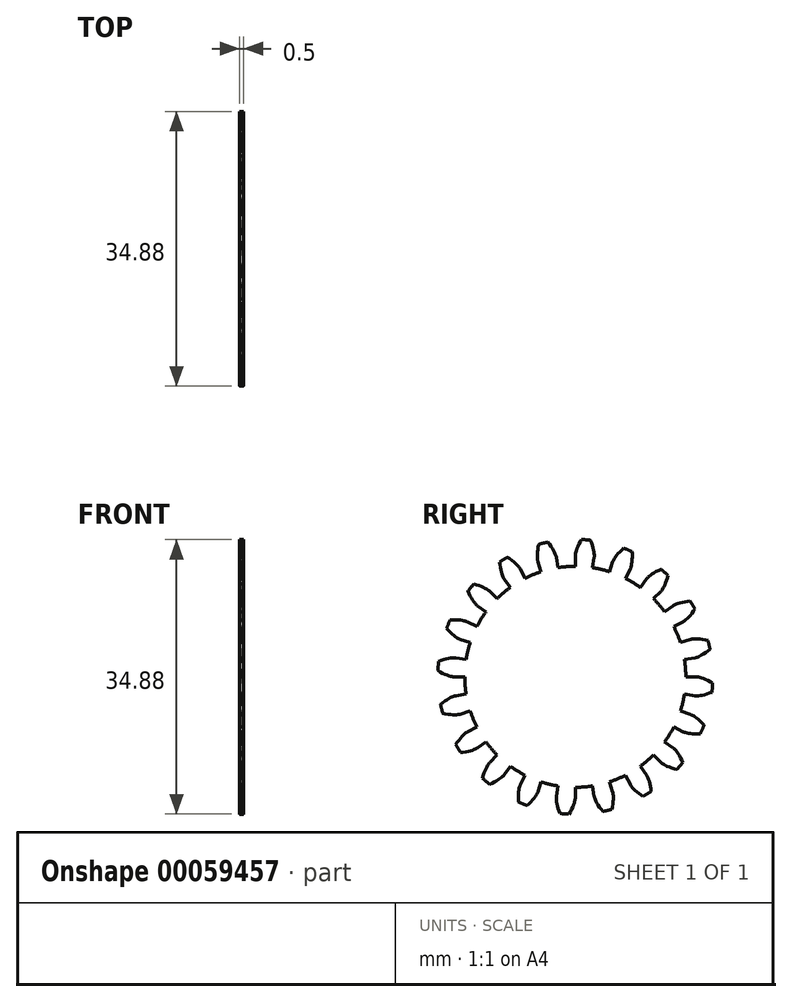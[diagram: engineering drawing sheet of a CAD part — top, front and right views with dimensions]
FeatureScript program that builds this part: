
annotation { "Feature Type Name" : "Feature", "Feature Type Description" : "" }
export const myFeature = defineFeature(function(context is Context, id is Id, definition is map)
    precondition{}
    {
        {
            assignVariable(context, id + "F0", {"name" : "GearThickness", "anyValue" : .5});
        }
        {
            var Q0;
            Q0=qCreatedBy(makeId("Right.planeOp"),FACE);
            var sketch = newSketch(context, id + "F1", { "sketchPlane" : qUnion([Q0])});
            skCircle(sketch, "E0", {"center": v(0, 0) * mm, "radius": 14.04 * mm});
            skCircle(sketch, "E1", {"center": v(0, 0) * mm, "radius": 15.37 * mm, "construction": true});
            skCircle(sketch, "E2", {"center": v(0, 0) * mm, "radius": 15.88 * mm, "construction": true});
            skCircle(sketch, "E3", {"center": v(0, 0) * mm, "radius": 17.46 * mm});
            skLineSegment(sketch, "E4", {"start": v(0, 0) * mm, "end": v(-15.37, 0) * mm, "construction": true});
            skLineSegment(sketch, "E5.1.0", {"start": v(0, 0) * mm, "end": v(-15.35, 0.77) * mm, "construction": true});
            skLineSegment(sketch, "E5.2.0", {"start": v(0, 0) * mm, "end": v(-15.3, 1.53) * mm, "construction": true});
            skLineSegment(sketch, "E5.3.0", {"start": v(0, 0) * mm, "end": v(-15.2, 2.3) * mm, "construction": true});
            skLineSegment(sketch, "E5.4.0", {"start": v(0, 0) * mm, "end": v(-15.06, 3.05) * mm, "construction": true});
            skLineSegment(sketch, "E5.5.0", {"start": v(0, 0) * mm, "end": v(-14.9, 3.8) * mm, "construction": true});
            skLineSegment(sketch, "E5.6.0", {"start": v(0, 0) * mm, "end": v(-14.68, 4.54) * mm, "construction": true});
            skLineSegment(sketch, "E5.7.0", {"start": v(0, 0) * mm, "end": v(-14.44, 5.27) * mm, "construction": true});
            skLineSegment(sketch, "E5.8.0", {"start": v(0, 0) * mm, "end": v(-14.16, 5.99) * mm, "construction": true});
            skLineSegment(sketch, "E5.9.0", {"start": v(0, 0) * mm, "end": v(-13.84, 6.69) * mm, "construction": true});
            skLineSegment(sketch, "E5.10.0", {"start": v(0, 0) * mm, "end": v(-13.49, 7.37) * mm, "construction": true});
            skLineSegment(sketch, "E5.11.0", {"start": v(0, 0) * mm, "end": v(-13.1, 8.03) * mm, "construction": true});
            skLineSegment(sketch, "E5.12.0", {"start": v(0, 0) * mm, "end": v(-12.68, 8.68) * mm, "construction": true});
            skLineSegment(sketch, "E5.13.0", {"start": v(0, 0) * mm, "end": v(-12.24, 9.3) * mm, "construction": true});
            skLineSegment(sketch, "E5.14.0", {"start": v(0, 0) * mm, "end": v(-11.76, 9.9) * mm, "construction": true});
            skLineSegment(sketch, "E5.anchor2", {"start": v(0, 0) * mm, "end": v(-11.76, 9.9) * mm, "construction": true});
            skLineSegment(sketch, "E6", {"start": v(-15.35, 0.77) * mm, "end": v(-15.39, 0) * mm, "construction": true});
            skLineSegment(sketch, "E7", {"start": v(-15.3, 1.53) * mm, "end": v(-15.45, 0) * mm, "construction": true});
            skLineSegment(sketch, "E8", {"start": v(-15.2, 2.3) * mm, "end": v(-15.54, 0.02) * mm, "construction": true});
            skLineSegment(sketch, "E9", {"start": v(-14.9, 3.8) * mm, "end": v(-15.84, 0.08) * mm, "construction": true});
            skLineSegment(sketch, "E10", {"start": v(-14.68, 4.54) * mm, "end": v(-16.05, 0.14) * mm, "construction": true});
            skLineSegment(sketch, "E11", {"start": v(-14.44, 5.27) * mm, "end": v(-16.28, 0.22) * mm, "construction": true});
            skLineSegment(sketch, "E12", {"start": v(-14.16, 5.99) * mm, "end": v(-16.55, 0.32) * mm, "construction": true});
            skLineSegment(sketch, "E13", {"start": v(-13.84, 6.69) * mm, "end": v(-16.85, 0.46) * mm, "construction": true});
            skLineSegment(sketch, "E14", {"start": v(-13.49, 7.37) * mm, "end": v(-17.17, 0.62) * mm, "construction": true});
            skLineSegment(sketch, "E15", {"start": v(-13.1, 8.03) * mm, "end": v(-17.52, 0.83) * mm, "construction": true});
            skLineSegment(sketch, "E16", {"start": v(-15.06, 3.05) * mm, "end": v(-15.67, 0.04) * mm, "construction": true});
            skLineSegment(sketch, "E17", {"start": v(-12.68, 8.68) * mm, "end": v(-17.9, 1.07) * mm, "construction": true});
            skLineSegment(sketch, "E18", {"start": v(-12.24, 9.3) * mm, "end": v(-18.28, 1.35) * mm, "construction": true});
            skLineSegment(sketch, "E19", {"start": v(-11.76, 9.9) * mm, "end": v(-18.69, 1.67) * mm, "construction": true});
            skLineSegment(sketch, "E20", {"start": v(0, 0) * mm, "end": v(-15.32, 1.2) * mm, "construction": true});
            skLineSegment(sketch, "E21", {"start": v(-14.04, 0) * mm, "end": v(-15.37, 0) * mm});
            skLineSegment(sketch, "E22.MirrorCS", {"start": v(-13.87, 2.2) * mm, "end": v(-15.18, 2.4) * mm});
            skLineSegment(sketch, "E23", {"start": v(-15.37, 0) * mm, "end": v(-15.39, 0) * mm});
            skLineSegment(sketch, "E24", {"start": v(-15.39, 0) * mm, "end": v(-15.45, 0) * mm});
            skLineSegment(sketch, "E25", {"start": v(-15.45, 0) * mm, "end": v(-15.54, 0.02) * mm});
            skLineSegment(sketch, "E26", {"start": v(-15.54, 0.02) * mm, "end": v(-15.67, 0.04) * mm});
            skLineSegment(sketch, "E27", {"start": v(-15.67, 0.04) * mm, "end": v(-15.84, 0.08) * mm});
            skLineSegment(sketch, "E28", {"start": v(-15.84, 0.08) * mm, "end": v(-16.05, 0.14) * mm});
            skLineSegment(sketch, "E29", {"start": v(-16.05, 0.14) * mm, "end": v(-16.28, 0.22) * mm});
            skLineSegment(sketch, "E30", {"start": v(-16.28, 0.22) * mm, "end": v(-16.55, 0.32) * mm});
            skLineSegment(sketch, "E31", {"start": v(-16.55, 0.32) * mm, "end": v(-16.85, 0.46) * mm});
            skLineSegment(sketch, "E32", {"start": v(-16.85, 0.46) * mm, "end": v(-17.17, 0.62) * mm});
            skLineSegment(sketch, "E33", {"start": v(-17.17, 0.62) * mm, "end": v(-17.52, 0.83) * mm});
            skLineSegment(sketch, "E34", {"start": v(-17.52, 0.83) * mm, "end": v(-17.9, 1.07) * mm});
            skLineSegment(sketch, "E35", {"start": v(-17.9, 1.07) * mm, "end": v(-18.28, 1.35) * mm});
            skLineSegment(sketch, "E36", {"start": v(-18.28, 1.35) * mm, "end": v(-18.69, 1.67) * mm});
            skLineSegment(sketch, "E37.MirrorCS", {"start": v(-15.18, 2.4) * mm, "end": v(-15.2, 2.4) * mm});
            skLineSegment(sketch, "E38.MirrorCS", {"start": v(-15.2, 2.4) * mm, "end": v(-15.26, 2.41) * mm});
            skLineSegment(sketch, "E39.MirrorCS", {"start": v(-15.26, 2.41) * mm, "end": v(-15.35, 2.41) * mm});
            skLineSegment(sketch, "E40.MirrorCS", {"start": v(-15.35, 2.41) * mm, "end": v(-15.49, 2.41) * mm});
            skLineSegment(sketch, "E41.MirrorCS", {"start": v(-15.66, 2.4) * mm, "end": v(-15.87, 2.37) * mm});
            skLineSegment(sketch, "E42.MirrorCS", {"start": v(-15.87, 2.37) * mm, "end": v(-16.12, 2.33) * mm});
            skLineSegment(sketch, "E43.MirrorCS", {"start": v(-16.12, 2.33) * mm, "end": v(-16.4, 2.27) * mm});
            skLineSegment(sketch, "E44.MirrorCS", {"start": v(-16.4, 2.27) * mm, "end": v(-16.71, 2.18) * mm});
            skLineSegment(sketch, "E45.MirrorCS", {"start": v(-17.06, 2.07) * mm, "end": v(-17.43, 1.92) * mm});
            skLineSegment(sketch, "E46.MirrorCS", {"start": v(-16.71, 2.18) * mm, "end": v(-17.06, 2.07) * mm});
            skLineSegment(sketch, "E47.MirrorCS", {"start": v(-17.43, 1.92) * mm, "end": v(-17.84, 1.74) * mm});
            skLineSegment(sketch, "E48.MirrorCS", {"start": v(-17.84, 1.74) * mm, "end": v(-18.27, 1.53) * mm});
            skLineSegment(sketch, "E49.MirrorCS", {"start": v(-18.27, 1.53) * mm, "end": v(-18.72, 1.27) * mm});
            skLineSegment(sketch, "E50.MirrorCS", {"start": v(-15.49, 2.41) * mm, "end": v(-15.66, 2.4) * mm});
            skLineSegment(sketch, "E51.1.0", {"start": v(-13.35, -4.34) * mm, "end": v(-14.62, -4.75) * mm});
            skLineSegment(sketch, "E51.1.1", {"start": v(-17.18, -3.56) * mm, "end": v(-17.5, -3.85) * mm});
            skLineSegment(sketch, "E51.1.2", {"start": v(-13.87, -2.2) * mm, "end": v(-15.18, -2.4) * mm});
            skLineSegment(sketch, "E51.1.3", {"start": v(-16.86, -3.3) * mm, "end": v(-17.18, -3.56) * mm});
            skLineSegment(sketch, "E51.1.4", {"start": v(-16.52, -4.71) * mm, "end": v(-16.92, -4.63) * mm});
            skLineSegment(sketch, "E51.1.5", {"start": v(-16.92, -4.63) * mm, "end": v(-17.35, -4.51) * mm});
            skLineSegment(sketch, "E51.1.6", {"start": v(-16.57, -3.09) * mm, "end": v(-16.86, -3.3) * mm});
            skLineSegment(sketch, "E51.1.7", {"start": v(-17.85, -4.2) * mm, "end": v(-18.2, -4.58) * mm});
            skLineSegment(sketch, "E51.1.8", {"start": v(-16.3, -2.9) * mm, "end": v(-16.57, -3.09) * mm});
            skLineSegment(sketch, "E51.1.9", {"start": v(-17.8, -4.37) * mm, "end": v(-18.29, -4.18) * mm});
            skLineSegment(sketch, "E51.1.10", {"start": v(-17.5, -3.85) * mm, "end": v(-17.85, -4.2) * mm});
            skLineSegment(sketch, "E51.1.11", {"start": v(-16.16, -4.77) * mm, "end": v(-16.52, -4.71) * mm});
            skLineSegment(sketch, "E51.1.12", {"start": v(-17.35, -4.51) * mm, "end": v(-17.8, -4.37) * mm});
            skLineSegment(sketch, "E51.1.13", {"start": v(-15.63, -2.56) * mm, "end": v(-15.83, -2.65) * mm});
            skLineSegment(sketch, "E51.1.14", {"start": v(-15.83, -2.65) * mm, "end": v(-16.05, -2.76) * mm});
            skLineSegment(sketch, "E51.1.15", {"start": v(-16.05, -2.76) * mm, "end": v(-16.3, -2.9) * mm});
            skLineSegment(sketch, "E51.1.16", {"start": v(-15.55, -4.83) * mm, "end": v(-15.84, -4.8) * mm});
            skLineSegment(sketch, "E51.1.17", {"start": v(-15.3, -4.83) * mm, "end": v(-15.55, -4.83) * mm});
            skLineSegment(sketch, "E51.1.18", {"start": v(-15.84, -4.8) * mm, "end": v(-16.16, -4.77) * mm});
            skLineSegment(sketch, "E51.1.19", {"start": v(-15.47, -2.5) * mm, "end": v(-15.63, -2.56) * mm});
            skLineSegment(sketch, "E51.1.20", {"start": v(-15.35, -2.45) * mm, "end": v(-15.47, -2.5) * mm});
            skLineSegment(sketch, "E51.1.21", {"start": v(-15.1, -4.82) * mm, "end": v(-15.3, -4.83) * mm});
            skLineSegment(sketch, "E51.1.22", {"start": v(-14.92, -4.8) * mm, "end": v(-15.1, -4.82) * mm});
            skLineSegment(sketch, "E51.1.23", {"start": v(-14.7, -4.77) * mm, "end": v(-14.79, -4.79) * mm});
            skLineSegment(sketch, "E51.1.24", {"start": v(-15.18, -2.4) * mm, "end": v(-15.2, -2.4) * mm});
            skLineSegment(sketch, "E51.1.25", {"start": v(-15.2, -2.4) * mm, "end": v(-15.26, -2.42) * mm});
            skLineSegment(sketch, "E51.1.26", {"start": v(-14.79, -4.79) * mm, "end": v(-14.92, -4.8) * mm});
            skLineSegment(sketch, "E51.1.27", {"start": v(-15.26, -2.42) * mm, "end": v(-15.35, -2.45) * mm});
            skLineSegment(sketch, "E51.1.28", {"start": v(-14.64, -4.75) * mm, "end": v(-14.7, -4.77) * mm});
            skLineSegment(sketch, "E51.1.29", {"start": v(-14.62, -4.75) * mm, "end": v(-14.64, -4.75) * mm});
            skLineSegment(sketch, "E51.2.0", {"start": v(-11.36, -8.25) * mm, "end": v(-12.43, -9.03) * mm});
            skLineSegment(sketch, "E51.2.1", {"start": v(-15.24, -8.7) * mm, "end": v(-15.46, -9.07) * mm});
            skLineSegment(sketch, "E51.2.2", {"start": v(-12.5, -6.37) * mm, "end": v(-13.7, -6.98) * mm});
            skLineSegment(sketch, "E51.2.3", {"start": v(-15.02, -8.35) * mm, "end": v(-15.24, -8.7) * mm});
            skLineSegment(sketch, "E51.2.4", {"start": v(-14.26, -9.59) * mm, "end": v(-14.66, -9.63) * mm});
            skLineSegment(sketch, "E51.2.5", {"start": v(-14.66, -9.63) * mm, "end": v(-15.1, -9.65) * mm});
            skLineSegment(sketch, "E51.2.6", {"start": v(-14.8, -8.06) * mm, "end": v(-15.02, -8.35) * mm});
            skLineSegment(sketch, "E51.2.7", {"start": v(-15.68, -9.5) * mm, "end": v(-15.89, -9.97) * mm});
            skLineSegment(sketch, "E51.2.8", {"start": v(-14.6, -7.8) * mm, "end": v(-14.8, -8.06) * mm});
            skLineSegment(sketch, "E51.2.9", {"start": v(-15.58, -9.65) * mm, "end": v(-16.1, -9.63) * mm});
            skLineSegment(sketch, "E51.2.10", {"start": v(-15.46, -9.07) * mm, "end": v(-15.68, -9.5) * mm});
            skLineSegment(sketch, "E51.2.11", {"start": v(-13.9, -9.53) * mm, "end": v(-14.26, -9.59) * mm});
            skLineSegment(sketch, "E51.2.12", {"start": v(-15.1, -9.65) * mm, "end": v(-15.58, -9.65) * mm});
            skLineSegment(sketch, "E51.2.13", {"start": v(-14.08, -7.26) * mm, "end": v(-14.23, -7.4) * mm});
            skLineSegment(sketch, "E51.2.14", {"start": v(-14.23, -7.4) * mm, "end": v(-14.4, -7.59) * mm});
            skLineSegment(sketch, "E51.2.15", {"start": v(-14.4, -7.59) * mm, "end": v(-14.6, -7.8) * mm});
            skLineSegment(sketch, "E51.2.16", {"start": v(-13.3, -9.4) * mm, "end": v(-13.58, -9.47) * mm});
            skLineSegment(sketch, "E51.2.17", {"start": v(-13.06, -9.32) * mm, "end": v(-13.3, -9.4) * mm});
            skLineSegment(sketch, "E51.2.18", {"start": v(-13.58, -9.47) * mm, "end": v(-13.9, -9.53) * mm});
            skLineSegment(sketch, "E51.2.19", {"start": v(-13.95, -7.15) * mm, "end": v(-14.08, -7.26) * mm});
            skLineSegment(sketch, "E51.2.20", {"start": v(-13.84, -7.07) * mm, "end": v(-13.95, -7.15) * mm});
            skLineSegment(sketch, "E51.2.21", {"start": v(-12.86, -9.25) * mm, "end": v(-13.06, -9.32) * mm});
            skLineSegment(sketch, "E51.2.22", {"start": v(-12.7, -9.18) * mm, "end": v(-12.86, -9.25) * mm});
            skLineSegment(sketch, "E51.2.23", {"start": v(-12.5, -9.07) * mm, "end": v(-12.58, -9.12) * mm});
            skLineSegment(sketch, "E51.2.24", {"start": v(-13.7, -6.98) * mm, "end": v(-13.71, -6.99) * mm});
            skLineSegment(sketch, "E51.2.25", {"start": v(-13.71, -6.99) * mm, "end": v(-13.76, -7.02) * mm});
            skLineSegment(sketch, "E51.2.26", {"start": v(-12.58, -9.12) * mm, "end": v(-12.7, -9.18) * mm});
            skLineSegment(sketch, "E51.2.27", {"start": v(-13.76, -7.02) * mm, "end": v(-13.84, -7.07) * mm});
            skLineSegment(sketch, "E51.2.28", {"start": v(-12.45, -9.04) * mm, "end": v(-12.5, -9.07) * mm});
            skLineSegment(sketch, "E51.2.29", {"start": v(-12.43, -9.03) * mm, "end": v(-12.45, -9.04) * mm});
            skLineSegment(sketch, "E51.3.0", {"start": v(-8.25, -11.36) * mm, "end": v(-9.03, -12.43) * mm});
            skLineSegment(sketch, "E51.3.1", {"start": v(-11.8, -12.97) * mm, "end": v(-11.9, -13.4) * mm});
            skLineSegment(sketch, "E51.3.2", {"start": v(-9.93, -9.93) * mm, "end": v(-10.87, -10.87) * mm});
            skLineSegment(sketch, "E51.3.3", {"start": v(-11.7, -12.58) * mm, "end": v(-11.8, -12.97) * mm});
            skLineSegment(sketch, "E51.3.4", {"start": v(-10.6, -13.53) * mm, "end": v(-10.97, -13.69) * mm});
            skLineSegment(sketch, "E51.3.5", {"start": v(-10.97, -13.69) * mm, "end": v(-11.38, -13.85) * mm});
            skLineSegment(sketch, "E51.3.6", {"start": v(-11.59, -12.24) * mm, "end": v(-11.7, -12.58) * mm});
            skLineSegment(sketch, "E51.3.7", {"start": v(-11.97, -13.88) * mm, "end": v(-12.03, -14.4) * mm});
            skLineSegment(sketch, "E51.3.8", {"start": v(-11.47, -11.93) * mm, "end": v(-11.59, -12.24) * mm});
            skLineSegment(sketch, "E51.3.9", {"start": v(-11.84, -14) * mm, "end": v(-12.34, -14.13) * mm});
            skLineSegment(sketch, "E51.3.10", {"start": v(-11.9, -13.4) * mm, "end": v(-11.97, -13.88) * mm});
            skLineSegment(sketch, "E51.3.11", {"start": v(-10.27, -13.36) * mm, "end": v(-10.6, -13.53) * mm});
            skLineSegment(sketch, "E51.3.12", {"start": v(-11.38, -13.85) * mm, "end": v(-11.84, -14) * mm});
            skLineSegment(sketch, "E51.3.13", {"start": v(-11.15, -11.26) * mm, "end": v(-11.25, -11.44) * mm});
            skLineSegment(sketch, "E51.3.14", {"start": v(-11.25, -11.44) * mm, "end": v(-11.36, -11.67) * mm});
            skLineSegment(sketch, "E51.3.15", {"start": v(-11.36, -11.67) * mm, "end": v(-11.47, -11.93) * mm});
            skLineSegment(sketch, "E51.3.16", {"start": v(-9.75, -13.04) * mm, "end": v(-9.99, -13.2) * mm});
            skLineSegment(sketch, "E51.3.17", {"start": v(-9.54, -12.9) * mm, "end": v(-9.75, -13.04) * mm});
            skLineSegment(sketch, "E51.3.18", {"start": v(-9.99, -13.2) * mm, "end": v(-10.27, -13.36) * mm});
            skLineSegment(sketch, "E51.3.19", {"start": v(-11.05, -11.11) * mm, "end": v(-11.15, -11.26) * mm});
            skLineSegment(sketch, "E51.3.20", {"start": v(-10.98, -11) * mm, "end": v(-11.05, -11.11) * mm});
            skLineSegment(sketch, "E51.3.21", {"start": v(-9.38, -12.77) * mm, "end": v(-9.54, -12.9) * mm});
            skLineSegment(sketch, "E51.3.22", {"start": v(-9.25, -12.66) * mm, "end": v(-9.38, -12.77) * mm});
            skLineSegment(sketch, "E51.3.23", {"start": v(-9.08, -12.5) * mm, "end": v(-9.15, -12.56) * mm});
            skLineSegment(sketch, "E51.3.24", {"start": v(-10.87, -10.87) * mm, "end": v(-10.88, -10.88) * mm});
            skLineSegment(sketch, "E51.3.25", {"start": v(-10.88, -10.88) * mm, "end": v(-10.92, -10.93) * mm});
            skLineSegment(sketch, "E51.3.26", {"start": v(-9.15, -12.56) * mm, "end": v(-9.25, -12.66) * mm});
            skLineSegment(sketch, "E51.3.27", {"start": v(-10.92, -10.93) * mm, "end": v(-10.98, -11) * mm});
            skLineSegment(sketch, "E51.3.28", {"start": v(-9.05, -12.45) * mm, "end": v(-9.08, -12.5) * mm});
            skLineSegment(sketch, "E51.3.29", {"start": v(-9.03, -12.43) * mm, "end": v(-9.05, -12.45) * mm});
            skLineSegment(sketch, "E51.4.0", {"start": v(-4.34, -13.35) * mm, "end": v(-4.75, -14.62) * mm});
            skLineSegment(sketch, "E51.4.1", {"start": v(-7.22, -15.99) * mm, "end": v(-7.17, -16.43) * mm});
            skLineSegment(sketch, "E51.4.2", {"start": v(-6.37, -12.5) * mm, "end": v(-6.98, -13.7) * mm});
            skLineSegment(sketch, "E51.4.3", {"start": v(-7.24, -15.58) * mm, "end": v(-7.22, -15.99) * mm});
            skLineSegment(sketch, "E51.4.4", {"start": v(-5.9, -16.14) * mm, "end": v(-6.2, -16.4) * mm});
            skLineSegment(sketch, "E51.4.5", {"start": v(-6.2, -16.4) * mm, "end": v(-6.54, -16.69) * mm});
            skLineSegment(sketch, "E51.4.6", {"start": v(-7.24, -15.22) * mm, "end": v(-7.24, -15.58) * mm});
            skLineSegment(sketch, "E51.4.7", {"start": v(-7.1, -16.9) * mm, "end": v(-7, -17.4) * mm});
            skLineSegment(sketch, "E51.4.8", {"start": v(-7.23, -14.9) * mm, "end": v(-7.24, -15.22) * mm});
            skLineSegment(sketch, "E51.4.9", {"start": v(-6.93, -16.97) * mm, "end": v(-7.37, -17.25) * mm});
            skLineSegment(sketch, "E51.4.10", {"start": v(-7.17, -16.43) * mm, "end": v(-7.1, -16.9) * mm});
            skLineSegment(sketch, "E51.4.11", {"start": v(-5.64, -15.88) * mm, "end": v(-5.9, -16.14) * mm});
            skLineSegment(sketch, "E51.4.12", {"start": v(-6.54, -16.69) * mm, "end": v(-6.93, -16.97) * mm});
            skLineSegment(sketch, "E51.4.13", {"start": v(-7.12, -14.15) * mm, "end": v(-7.16, -14.36) * mm});
            skLineSegment(sketch, "E51.4.14", {"start": v(-7.16, -14.36) * mm, "end": v(-7.2, -14.6) * mm});
            skLineSegment(sketch, "E51.4.15", {"start": v(-7.2, -14.6) * mm, "end": v(-7.23, -14.9) * mm});
            skLineSegment(sketch, "E51.4.16", {"start": v(-5.24, -15.42) * mm, "end": v(-5.42, -15.64) * mm});
            skLineSegment(sketch, "E51.4.17", {"start": v(-5.09, -15.22) * mm, "end": v(-5.24, -15.42) * mm});
            skLineSegment(sketch, "E51.4.18", {"start": v(-5.42, -15.64) * mm, "end": v(-5.64, -15.88) * mm});
            skLineSegment(sketch, "E51.4.19", {"start": v(-7.08, -13.98) * mm, "end": v(-7.12, -14.15) * mm});
            skLineSegment(sketch, "E51.4.20", {"start": v(-7.04, -13.86) * mm, "end": v(-7.08, -13.98) * mm});
            skLineSegment(sketch, "E51.4.21", {"start": v(-4.97, -15.04) * mm, "end": v(-5.09, -15.22) * mm});
            skLineSegment(sketch, "E51.4.22", {"start": v(-4.88, -14.9) * mm, "end": v(-4.97, -15.04) * mm});
            skLineSegment(sketch, "E51.4.23", {"start": v(-4.78, -14.69) * mm, "end": v(-4.82, -14.78) * mm});
            skLineSegment(sketch, "E51.4.24", {"start": v(-6.98, -13.7) * mm, "end": v(-6.99, -13.71) * mm});
            skLineSegment(sketch, "E51.4.25", {"start": v(-6.99, -13.71) * mm, "end": v(-7, -13.76) * mm});
            skLineSegment(sketch, "E51.4.26", {"start": v(-4.82, -14.78) * mm, "end": v(-4.88, -14.9) * mm});
            skLineSegment(sketch, "E51.4.27", {"start": v(-7, -13.76) * mm, "end": v(-7.04, -13.86) * mm});
            skLineSegment(sketch, "E51.4.28", {"start": v(-4.76, -14.64) * mm, "end": v(-4.78, -14.69) * mm});
            skLineSegment(sketch, "E51.4.29", {"start": v(-4.75, -14.62) * mm, "end": v(-4.76, -14.64) * mm});
            skLineSegment(sketch, "E51.5.0", {"start": v(0, -14.04) * mm, "end": v(0, -15.37) * mm});
            skLineSegment(sketch, "E51.5.1", {"start": v(-1.92, -17.43) * mm, "end": v(-1.74, -17.84) * mm});
            skLineSegment(sketch, "E51.5.2", {"start": v(-2.2, -13.87) * mm, "end": v(-2.4, -15.18) * mm});
            skLineSegment(sketch, "E51.5.3", {"start": v(-2.07, -17.06) * mm, "end": v(-1.92, -17.43) * mm});
            skLineSegment(sketch, "E51.5.4", {"start": v(-0.62, -17.17) * mm, "end": v(-0.83, -17.52) * mm});
            skLineSegment(sketch, "E51.5.5", {"start": v(-0.83, -17.52) * mm, "end": v(-1.07, -17.9) * mm});
            skLineSegment(sketch, "E51.5.6", {"start": v(-2.18, -16.71) * mm, "end": v(-2.07, -17.06) * mm});
            skLineSegment(sketch, "E51.5.7", {"start": v(-1.53, -18.27) * mm, "end": v(-1.27, -18.72) * mm});
            skLineSegment(sketch, "E51.5.8", {"start": v(-2.27, -16.4) * mm, "end": v(-2.18, -16.71) * mm});
            skLineSegment(sketch, "E51.5.9", {"start": v(-1.35, -18.28) * mm, "end": v(-1.67, -18.69) * mm});
            skLineSegment(sketch, "E51.5.10", {"start": v(-1.74, -17.84) * mm, "end": v(-1.53, -18.27) * mm});
            skLineSegment(sketch, "E51.5.11", {"start": v(-0.46, -16.85) * mm, "end": v(-0.62, -17.17) * mm});
            skLineSegment(sketch, "E51.5.12", {"start": v(-1.07, -17.9) * mm, "end": v(-1.35, -18.28) * mm});
            skLineSegment(sketch, "E51.5.13", {"start": v(-2.4, -15.66) * mm, "end": v(-2.37, -15.87) * mm});
            skLineSegment(sketch, "E51.5.14", {"start": v(-2.37, -15.87) * mm, "end": v(-2.33, -16.12) * mm});
            skLineSegment(sketch, "E51.5.15", {"start": v(-2.33, -16.12) * mm, "end": v(-2.27, -16.4) * mm});
            skLineSegment(sketch, "E51.5.16", {"start": v(-0.22, -16.28) * mm, "end": v(-0.32, -16.55) * mm});
            skLineSegment(sketch, "E51.5.17", {"start": v(-0.14, -16.05) * mm, "end": v(-0.22, -16.28) * mm});
            skLineSegment(sketch, "E51.5.18", {"start": v(-0.32, -16.55) * mm, "end": v(-0.46, -16.85) * mm});
            skLineSegment(sketch, "E51.5.19", {"start": v(-2.41, -15.49) * mm, "end": v(-2.4, -15.66) * mm});
            skLineSegment(sketch, "E51.5.20", {"start": v(-2.41, -15.35) * mm, "end": v(-2.41, -15.49) * mm});
            skLineSegment(sketch, "E51.5.21", {"start": v(-0.08, -15.84) * mm, "end": v(-0.14, -16.05) * mm});
            skLineSegment(sketch, "E51.5.22", {"start": v(-0.04, -15.67) * mm, "end": v(-0.08, -15.84) * mm});
            skLineSegment(sketch, "E51.5.23", {"start": v(0, -15.45) * mm, "end": v(-0.02, -15.54) * mm});
            skLineSegment(sketch, "E51.5.24", {"start": v(-2.4, -15.18) * mm, "end": v(-2.4, -15.2) * mm});
            skLineSegment(sketch, "E51.5.25", {"start": v(-2.4, -15.2) * mm, "end": v(-2.41, -15.26) * mm});
            skLineSegment(sketch, "E51.5.26", {"start": v(-0.02, -15.54) * mm, "end": v(-0.04, -15.67) * mm});
            skLineSegment(sketch, "E51.5.27", {"start": v(-2.41, -15.26) * mm, "end": v(-2.41, -15.35) * mm});
            skLineSegment(sketch, "E51.5.28", {"start": v(0, -15.39) * mm, "end": v(0, -15.45) * mm});
            skLineSegment(sketch, "E51.5.29", {"start": v(0, -15.37) * mm, "end": v(0, -15.39) * mm});
            skLineSegment(sketch, "E51.6.0", {"start": v(4.34, -13.35) * mm, "end": v(4.75, -14.62) * mm});
            skLineSegment(sketch, "E51.6.1", {"start": v(3.56, -17.18) * mm, "end": v(3.85, -17.5) * mm});
            skLineSegment(sketch, "E51.6.2", {"start": v(2.2, -13.87) * mm, "end": v(2.4, -15.18) * mm});
            skLineSegment(sketch, "E51.6.3", {"start": v(3.3, -16.86) * mm, "end": v(3.56, -17.18) * mm});
            skLineSegment(sketch, "E51.6.4", {"start": v(4.71, -16.52) * mm, "end": v(4.63, -16.92) * mm});
            skLineSegment(sketch, "E51.6.5", {"start": v(4.63, -16.92) * mm, "end": v(4.51, -17.35) * mm});
            skLineSegment(sketch, "E51.6.6", {"start": v(3.09, -16.57) * mm, "end": v(3.3, -16.86) * mm});
            skLineSegment(sketch, "E51.6.7", {"start": v(4.2, -17.85) * mm, "end": v(4.58, -18.2) * mm});
            skLineSegment(sketch, "E51.6.8", {"start": v(2.9, -16.3) * mm, "end": v(3.09, -16.57) * mm});
            skLineSegment(sketch, "E51.6.9", {"start": v(4.37, -17.8) * mm, "end": v(4.18, -18.29) * mm});
            skLineSegment(sketch, "E51.6.10", {"start": v(3.85, -17.5) * mm, "end": v(4.2, -17.85) * mm});
            skLineSegment(sketch, "E51.6.11", {"start": v(4.77, -16.16) * mm, "end": v(4.71, -16.52) * mm});
            skLineSegment(sketch, "E51.6.12", {"start": v(4.51, -17.35) * mm, "end": v(4.37, -17.8) * mm});
            skLineSegment(sketch, "E51.6.13", {"start": v(2.56, -15.63) * mm, "end": v(2.65, -15.83) * mm});
            skLineSegment(sketch, "E51.6.14", {"start": v(2.65, -15.83) * mm, "end": v(2.76, -16.05) * mm});
            skLineSegment(sketch, "E51.6.15", {"start": v(2.76, -16.05) * mm, "end": v(2.9, -16.3) * mm});
            skLineSegment(sketch, "E51.6.16", {"start": v(4.83, -15.55) * mm, "end": v(4.8, -15.84) * mm});
            skLineSegment(sketch, "E51.6.17", {"start": v(4.83, -15.3) * mm, "end": v(4.83, -15.55) * mm});
            skLineSegment(sketch, "E51.6.18", {"start": v(4.8, -15.84) * mm, "end": v(4.77, -16.16) * mm});
            skLineSegment(sketch, "E51.6.19", {"start": v(2.5, -15.47) * mm, "end": v(2.56, -15.63) * mm});
            skLineSegment(sketch, "E51.6.20", {"start": v(2.45, -15.35) * mm, "end": v(2.5, -15.47) * mm});
            skLineSegment(sketch, "E51.6.21", {"start": v(4.82, -15.1) * mm, "end": v(4.83, -15.3) * mm});
            skLineSegment(sketch, "E51.6.22", {"start": v(4.8, -14.92) * mm, "end": v(4.82, -15.1) * mm});
            skLineSegment(sketch, "E51.6.23", {"start": v(4.77, -14.7) * mm, "end": v(4.79, -14.79) * mm});
            skLineSegment(sketch, "E51.6.24", {"start": v(2.4, -15.18) * mm, "end": v(2.4, -15.2) * mm});
            skLineSegment(sketch, "E51.6.25", {"start": v(2.4, -15.2) * mm, "end": v(2.42, -15.26) * mm});
            skLineSegment(sketch, "E51.6.26", {"start": v(4.79, -14.79) * mm, "end": v(4.8, -14.92) * mm});
            skLineSegment(sketch, "E51.6.27", {"start": v(2.42, -15.26) * mm, "end": v(2.45, -15.35) * mm});
            skLineSegment(sketch, "E51.6.28", {"start": v(4.75, -14.64) * mm, "end": v(4.77, -14.7) * mm});
            skLineSegment(sketch, "E51.6.29", {"start": v(4.75, -14.62) * mm, "end": v(4.75, -14.64) * mm});
            skLineSegment(sketch, "E51.7.0", {"start": v(8.25, -11.36) * mm, "end": v(9.03, -12.43) * mm});
            skLineSegment(sketch, "E51.7.1", {"start": v(8.7, -15.24) * mm, "end": v(9.07, -15.46) * mm});
            skLineSegment(sketch, "E51.7.2", {"start": v(6.37, -12.5) * mm, "end": v(6.98, -13.7) * mm});
            skLineSegment(sketch, "E51.7.3", {"start": v(8.35, -15.02) * mm, "end": v(8.7, -15.24) * mm});
            skLineSegment(sketch, "E51.7.4", {"start": v(9.59, -14.26) * mm, "end": v(9.63, -14.66) * mm});
            skLineSegment(sketch, "E51.7.5", {"start": v(9.63, -14.66) * mm, "end": v(9.65, -15.1) * mm});
            skLineSegment(sketch, "E51.7.6", {"start": v(8.06, -14.8) * mm, "end": v(8.35, -15.02) * mm});
            skLineSegment(sketch, "E51.7.7", {"start": v(9.5, -15.68) * mm, "end": v(9.97, -15.89) * mm});
            skLineSegment(sketch, "E51.7.8", {"start": v(7.8, -14.6) * mm, "end": v(8.06, -14.8) * mm});
            skLineSegment(sketch, "E51.7.9", {"start": v(9.65, -15.58) * mm, "end": v(9.63, -16.1) * mm});
            skLineSegment(sketch, "E51.7.10", {"start": v(9.07, -15.46) * mm, "end": v(9.5, -15.68) * mm});
            skLineSegment(sketch, "E51.7.11", {"start": v(9.53, -13.9) * mm, "end": v(9.59, -14.26) * mm});
            skLineSegment(sketch, "E51.7.12", {"start": v(9.65, -15.1) * mm, "end": v(9.65, -15.58) * mm});
            skLineSegment(sketch, "E51.7.13", {"start": v(7.26, -14.08) * mm, "end": v(7.4, -14.23) * mm});
            skLineSegment(sketch, "E51.7.14", {"start": v(7.4, -14.23) * mm, "end": v(7.59, -14.4) * mm});
            skLineSegment(sketch, "E51.7.15", {"start": v(7.59, -14.4) * mm, "end": v(7.8, -14.6) * mm});
            skLineSegment(sketch, "E51.7.16", {"start": v(9.4, -13.3) * mm, "end": v(9.47, -13.58) * mm});
            skLineSegment(sketch, "E51.7.17", {"start": v(9.32, -13.06) * mm, "end": v(9.4, -13.3) * mm});
            skLineSegment(sketch, "E51.7.18", {"start": v(9.47, -13.58) * mm, "end": v(9.53, -13.9) * mm});
            skLineSegment(sketch, "E51.7.19", {"start": v(7.15, -13.95) * mm, "end": v(7.26, -14.08) * mm});
            skLineSegment(sketch, "E51.7.20", {"start": v(7.07, -13.84) * mm, "end": v(7.15, -13.95) * mm});
            skLineSegment(sketch, "E51.7.21", {"start": v(9.25, -12.86) * mm, "end": v(9.32, -13.06) * mm});
            skLineSegment(sketch, "E51.7.22", {"start": v(9.18, -12.7) * mm, "end": v(9.25, -12.86) * mm});
            skLineSegment(sketch, "E51.7.23", {"start": v(9.07, -12.5) * mm, "end": v(9.12, -12.58) * mm});
            skLineSegment(sketch, "E51.7.24", {"start": v(6.98, -13.7) * mm, "end": v(6.99, -13.71) * mm});
            skLineSegment(sketch, "E51.7.25", {"start": v(6.99, -13.71) * mm, "end": v(7.02, -13.76) * mm});
            skLineSegment(sketch, "E51.7.26", {"start": v(9.12, -12.58) * mm, "end": v(9.18, -12.7) * mm});
            skLineSegment(sketch, "E51.7.27", {"start": v(7.02, -13.76) * mm, "end": v(7.07, -13.84) * mm});
            skLineSegment(sketch, "E51.7.28", {"start": v(9.04, -12.45) * mm, "end": v(9.07, -12.5) * mm});
            skLineSegment(sketch, "E51.7.29", {"start": v(9.03, -12.43) * mm, "end": v(9.04, -12.45) * mm});
            skLineSegment(sketch, "E51.8.0", {"start": v(11.36, -8.25) * mm, "end": v(12.43, -9.03) * mm});
            skLineSegment(sketch, "E51.8.1", {"start": v(12.97, -11.8) * mm, "end": v(13.4, -11.9) * mm});
            skLineSegment(sketch, "E51.8.2", {"start": v(9.93, -9.93) * mm, "end": v(10.87, -10.87) * mm});
            skLineSegment(sketch, "E51.8.3", {"start": v(12.58, -11.7) * mm, "end": v(12.97, -11.8) * mm});
            skLineSegment(sketch, "E51.8.4", {"start": v(13.53, -10.6) * mm, "end": v(13.69, -10.97) * mm});
            skLineSegment(sketch, "E51.8.5", {"start": v(13.69, -10.97) * mm, "end": v(13.85, -11.38) * mm});
            skLineSegment(sketch, "E51.8.6", {"start": v(12.24, -11.59) * mm, "end": v(12.58, -11.7) * mm});
            skLineSegment(sketch, "E51.8.7", {"start": v(13.88, -11.97) * mm, "end": v(14.4, -12.03) * mm});
            skLineSegment(sketch, "E51.8.8", {"start": v(11.93, -11.47) * mm, "end": v(12.24, -11.59) * mm});
            skLineSegment(sketch, "E51.8.9", {"start": v(14, -11.84) * mm, "end": v(14.13, -12.34) * mm});
            skLineSegment(sketch, "E51.8.10", {"start": v(13.4, -11.9) * mm, "end": v(13.88, -11.97) * mm});
            skLineSegment(sketch, "E51.8.11", {"start": v(13.36, -10.27) * mm, "end": v(13.53, -10.6) * mm});
            skLineSegment(sketch, "E51.8.12", {"start": v(13.85, -11.38) * mm, "end": v(14, -11.84) * mm});
            skLineSegment(sketch, "E51.8.13", {"start": v(11.26, -11.15) * mm, "end": v(11.44, -11.25) * mm});
            skLineSegment(sketch, "E51.8.14", {"start": v(11.44, -11.25) * mm, "end": v(11.67, -11.36) * mm});
            skLineSegment(sketch, "E51.8.15", {"start": v(11.67, -11.36) * mm, "end": v(11.93, -11.47) * mm});
            skLineSegment(sketch, "E51.8.16", {"start": v(13.04, -9.75) * mm, "end": v(13.2, -9.99) * mm});
            skLineSegment(sketch, "E51.8.17", {"start": v(12.9, -9.54) * mm, "end": v(13.04, -9.75) * mm});
            skLineSegment(sketch, "E51.8.18", {"start": v(13.2, -9.99) * mm, "end": v(13.36, -10.27) * mm});
            skLineSegment(sketch, "E51.8.19", {"start": v(11.11, -11.05) * mm, "end": v(11.26, -11.15) * mm});
            skLineSegment(sketch, "E51.8.20", {"start": v(11, -10.98) * mm, "end": v(11.11, -11.05) * mm});
            skLineSegment(sketch, "E51.8.21", {"start": v(12.77, -9.38) * mm, "end": v(12.9, -9.54) * mm});
            skLineSegment(sketch, "E51.8.22", {"start": v(12.66, -9.25) * mm, "end": v(12.77, -9.38) * mm});
            skLineSegment(sketch, "E51.8.23", {"start": v(12.5, -9.08) * mm, "end": v(12.56, -9.15) * mm});
            skLineSegment(sketch, "E51.8.24", {"start": v(10.87, -10.87) * mm, "end": v(10.88, -10.88) * mm});
            skLineSegment(sketch, "E51.8.25", {"start": v(10.88, -10.88) * mm, "end": v(10.93, -10.92) * mm});
            skLineSegment(sketch, "E51.8.26", {"start": v(12.56, -9.15) * mm, "end": v(12.66, -9.25) * mm});
            skLineSegment(sketch, "E51.8.27", {"start": v(10.93, -10.92) * mm, "end": v(11, -10.98) * mm});
            skLineSegment(sketch, "E51.8.28", {"start": v(12.45, -9.05) * mm, "end": v(12.5, -9.08) * mm});
            skLineSegment(sketch, "E51.8.29", {"start": v(12.43, -9.03) * mm, "end": v(12.45, -9.05) * mm});
            skLineSegment(sketch, "E51.9.0", {"start": v(13.35, -4.34) * mm, "end": v(14.62, -4.75) * mm});
            skLineSegment(sketch, "E51.9.1", {"start": v(15.99, -7.22) * mm, "end": v(16.43, -7.17) * mm});
            skLineSegment(sketch, "E51.9.2", {"start": v(12.5, -6.37) * mm, "end": v(13.7, -6.98) * mm});
            skLineSegment(sketch, "E51.9.3", {"start": v(15.58, -7.24) * mm, "end": v(15.99, -7.22) * mm});
            skLineSegment(sketch, "E51.9.4", {"start": v(16.14, -5.9) * mm, "end": v(16.4, -6.2) * mm});
            skLineSegment(sketch, "E51.9.5", {"start": v(16.4, -6.2) * mm, "end": v(16.69, -6.54) * mm});
            skLineSegment(sketch, "E51.9.6", {"start": v(15.22, -7.24) * mm, "end": v(15.58, -7.24) * mm});
            skLineSegment(sketch, "E51.9.7", {"start": v(16.9, -7.1) * mm, "end": v(17.4, -7) * mm});
            skLineSegment(sketch, "E51.9.8", {"start": v(14.9, -7.23) * mm, "end": v(15.22, -7.24) * mm});
            skLineSegment(sketch, "E51.9.9", {"start": v(16.97, -6.93) * mm, "end": v(17.25, -7.37) * mm});
            skLineSegment(sketch, "E51.9.10", {"start": v(16.43, -7.17) * mm, "end": v(16.9, -7.1) * mm});
            skLineSegment(sketch, "E51.9.11", {"start": v(15.88, -5.64) * mm, "end": v(16.14, -5.9) * mm});
            skLineSegment(sketch, "E51.9.12", {"start": v(16.69, -6.54) * mm, "end": v(16.97, -6.93) * mm});
            skLineSegment(sketch, "E51.9.13", {"start": v(14.15, -7.12) * mm, "end": v(14.36, -7.16) * mm});
            skLineSegment(sketch, "E51.9.14", {"start": v(14.36, -7.16) * mm, "end": v(14.6, -7.2) * mm});
            skLineSegment(sketch, "E51.9.15", {"start": v(14.6, -7.2) * mm, "end": v(14.9, -7.23) * mm});
            skLineSegment(sketch, "E51.9.16", {"start": v(15.42, -5.24) * mm, "end": v(15.64, -5.42) * mm});
            skLineSegment(sketch, "E51.9.17", {"start": v(15.22, -5.09) * mm, "end": v(15.42, -5.24) * mm});
            skLineSegment(sketch, "E51.9.18", {"start": v(15.64, -5.42) * mm, "end": v(15.88, -5.64) * mm});
            skLineSegment(sketch, "E51.9.19", {"start": v(13.98, -7.08) * mm, "end": v(14.15, -7.12) * mm});
            skLineSegment(sketch, "E51.9.20", {"start": v(13.86, -7.04) * mm, "end": v(13.98, -7.08) * mm});
            skLineSegment(sketch, "E51.9.21", {"start": v(15.04, -4.97) * mm, "end": v(15.22, -5.09) * mm});
            skLineSegment(sketch, "E51.9.22", {"start": v(14.9, -4.88) * mm, "end": v(15.04, -4.97) * mm});
            skLineSegment(sketch, "E51.9.23", {"start": v(14.69, -4.78) * mm, "end": v(14.78, -4.82) * mm});
            skLineSegment(sketch, "E51.9.24", {"start": v(13.7, -6.98) * mm, "end": v(13.71, -6.99) * mm});
            skLineSegment(sketch, "E51.9.25", {"start": v(13.71, -6.99) * mm, "end": v(13.76, -7) * mm});
            skLineSegment(sketch, "E51.9.26", {"start": v(14.78, -4.82) * mm, "end": v(14.9, -4.88) * mm});
            skLineSegment(sketch, "E51.9.27", {"start": v(13.76, -7) * mm, "end": v(13.86, -7.04) * mm});
            skLineSegment(sketch, "E51.9.28", {"start": v(14.64, -4.76) * mm, "end": v(14.69, -4.78) * mm});
            skLineSegment(sketch, "E51.9.29", {"start": v(14.62, -4.75) * mm, "end": v(14.64, -4.76) * mm});
            skLineSegment(sketch, "E51.10.0", {"start": v(14.04, 0) * mm, "end": v(15.37, 0) * mm});
            skLineSegment(sketch, "E51.10.1", {"start": v(17.43, -1.92) * mm, "end": v(17.84, -1.74) * mm});
            skLineSegment(sketch, "E51.10.2", {"start": v(13.87, -2.2) * mm, "end": v(15.18, -2.4) * mm});
            skLineSegment(sketch, "E51.10.3", {"start": v(17.06, -2.07) * mm, "end": v(17.43, -1.92) * mm});
            skLineSegment(sketch, "E51.10.4", {"start": v(17.17, -0.62) * mm, "end": v(17.52, -0.83) * mm});
            skLineSegment(sketch, "E51.10.5", {"start": v(17.52, -0.83) * mm, "end": v(17.9, -1.07) * mm});
            skLineSegment(sketch, "E51.10.6", {"start": v(16.71, -2.18) * mm, "end": v(17.06, -2.07) * mm});
            skLineSegment(sketch, "E51.10.7", {"start": v(18.27, -1.53) * mm, "end": v(18.72, -1.27) * mm});
            skLineSegment(sketch, "E51.10.8", {"start": v(16.4, -2.27) * mm, "end": v(16.71, -2.18) * mm});
            skLineSegment(sketch, "E51.10.9", {"start": v(18.28, -1.35) * mm, "end": v(18.69, -1.67) * mm});
            skLineSegment(sketch, "E51.10.10", {"start": v(17.84, -1.74) * mm, "end": v(18.27, -1.53) * mm});
            skLineSegment(sketch, "E51.10.11", {"start": v(16.85, -0.46) * mm, "end": v(17.17, -0.62) * mm});
            skLineSegment(sketch, "E51.10.12", {"start": v(17.9, -1.07) * mm, "end": v(18.28, -1.35) * mm});
            skLineSegment(sketch, "E51.10.13", {"start": v(15.66, -2.4) * mm, "end": v(15.87, -2.37) * mm});
            skLineSegment(sketch, "E51.10.14", {"start": v(15.87, -2.37) * mm, "end": v(16.12, -2.33) * mm});
            skLineSegment(sketch, "E51.10.15", {"start": v(16.12, -2.33) * mm, "end": v(16.4, -2.27) * mm});
            skLineSegment(sketch, "E51.10.16", {"start": v(16.28, -0.22) * mm, "end": v(16.55, -0.32) * mm});
            skLineSegment(sketch, "E51.10.17", {"start": v(16.05, -0.14) * mm, "end": v(16.28, -0.22) * mm});
            skLineSegment(sketch, "E51.10.18", {"start": v(16.55, -0.32) * mm, "end": v(16.85, -0.46) * mm});
            skLineSegment(sketch, "E51.10.19", {"start": v(15.49, -2.41) * mm, "end": v(15.66, -2.4) * mm});
            skLineSegment(sketch, "E51.10.20", {"start": v(15.35, -2.41) * mm, "end": v(15.49, -2.41) * mm});
            skLineSegment(sketch, "E51.10.21", {"start": v(15.84, -0.08) * mm, "end": v(16.05, -0.14) * mm});
            skLineSegment(sketch, "E51.10.22", {"start": v(15.67, -0.04) * mm, "end": v(15.84, -0.08) * mm});
            skLineSegment(sketch, "E51.10.23", {"start": v(15.45, 0) * mm, "end": v(15.54, -0.02) * mm});
            skLineSegment(sketch, "E51.10.24", {"start": v(15.18, -2.4) * mm, "end": v(15.2, -2.4) * mm});
            skLineSegment(sketch, "E51.10.25", {"start": v(15.2, -2.4) * mm, "end": v(15.26, -2.41) * mm});
            skLineSegment(sketch, "E51.10.26", {"start": v(15.54, -0.02) * mm, "end": v(15.67, -0.04) * mm});
            skLineSegment(sketch, "E51.10.27", {"start": v(15.26, -2.41) * mm, "end": v(15.35, -2.41) * mm});
            skLineSegment(sketch, "E51.10.28", {"start": v(15.39, 0) * mm, "end": v(15.45, 0) * mm});
            skLineSegment(sketch, "E51.10.29", {"start": v(15.37, 0) * mm, "end": v(15.39, 0) * mm});
            skLineSegment(sketch, "E51.11.0", {"start": v(13.35, 4.34) * mm, "end": v(14.62, 4.75) * mm});
            skLineSegment(sketch, "E51.11.1", {"start": v(17.18, 3.56) * mm, "end": v(17.5, 3.85) * mm});
            skLineSegment(sketch, "E51.11.2", {"start": v(13.87, 2.2) * mm, "end": v(15.18, 2.4) * mm});
            skLineSegment(sketch, "E51.11.3", {"start": v(16.86, 3.3) * mm, "end": v(17.18, 3.56) * mm});
            skLineSegment(sketch, "E51.11.4", {"start": v(16.52, 4.71) * mm, "end": v(16.92, 4.63) * mm});
            skLineSegment(sketch, "E51.11.5", {"start": v(16.92, 4.63) * mm, "end": v(17.35, 4.51) * mm});
            skLineSegment(sketch, "E51.11.6", {"start": v(16.57, 3.09) * mm, "end": v(16.86, 3.3) * mm});
            skLineSegment(sketch, "E51.11.7", {"start": v(17.85, 4.2) * mm, "end": v(18.2, 4.58) * mm});
            skLineSegment(sketch, "E51.11.8", {"start": v(16.3, 2.9) * mm, "end": v(16.57, 3.09) * mm});
            skLineSegment(sketch, "E51.11.9", {"start": v(17.8, 4.37) * mm, "end": v(18.29, 4.18) * mm});
            skLineSegment(sketch, "E51.11.10", {"start": v(17.5, 3.85) * mm, "end": v(17.85, 4.2) * mm});
            skLineSegment(sketch, "E51.11.11", {"start": v(16.16, 4.77) * mm, "end": v(16.52, 4.71) * mm});
            skLineSegment(sketch, "E51.11.12", {"start": v(17.35, 4.51) * mm, "end": v(17.8, 4.37) * mm});
            skLineSegment(sketch, "E51.11.13", {"start": v(15.63, 2.56) * mm, "end": v(15.83, 2.65) * mm});
            skLineSegment(sketch, "E51.11.14", {"start": v(15.83, 2.65) * mm, "end": v(16.05, 2.76) * mm});
            skLineSegment(sketch, "E51.11.15", {"start": v(16.05, 2.76) * mm, "end": v(16.3, 2.9) * mm});
            skLineSegment(sketch, "E51.11.16", {"start": v(15.55, 4.83) * mm, "end": v(15.84, 4.8) * mm});
            skLineSegment(sketch, "E51.11.17", {"start": v(15.3, 4.83) * mm, "end": v(15.55, 4.83) * mm});
            skLineSegment(sketch, "E51.11.18", {"start": v(15.84, 4.8) * mm, "end": v(16.16, 4.77) * mm});
            skLineSegment(sketch, "E51.11.19", {"start": v(15.47, 2.5) * mm, "end": v(15.63, 2.56) * mm});
            skLineSegment(sketch, "E51.11.20", {"start": v(15.35, 2.45) * mm, "end": v(15.47, 2.5) * mm});
            skLineSegment(sketch, "E51.11.21", {"start": v(15.1, 4.82) * mm, "end": v(15.3, 4.83) * mm});
            skLineSegment(sketch, "E51.11.22", {"start": v(14.92, 4.8) * mm, "end": v(15.1, 4.82) * mm});
            skLineSegment(sketch, "E51.11.23", {"start": v(14.7, 4.77) * mm, "end": v(14.79, 4.79) * mm});
            skLineSegment(sketch, "E51.11.24", {"start": v(15.18, 2.4) * mm, "end": v(15.2, 2.4) * mm});
            skLineSegment(sketch, "E51.11.25", {"start": v(15.2, 2.4) * mm, "end": v(15.26, 2.42) * mm});
            skLineSegment(sketch, "E51.11.26", {"start": v(14.79, 4.79) * mm, "end": v(14.92, 4.8) * mm});
            skLineSegment(sketch, "E51.11.27", {"start": v(15.26, 2.42) * mm, "end": v(15.35, 2.45) * mm});
            skLineSegment(sketch, "E51.11.28", {"start": v(14.64, 4.75) * mm, "end": v(14.7, 4.77) * mm});
            skLineSegment(sketch, "E51.11.29", {"start": v(14.62, 4.75) * mm, "end": v(14.64, 4.75) * mm});
            skLineSegment(sketch, "E51.12.0", {"start": v(11.36, 8.25) * mm, "end": v(12.43, 9.03) * mm});
            skLineSegment(sketch, "E51.12.1", {"start": v(15.24, 8.7) * mm, "end": v(15.46, 9.07) * mm});
            skLineSegment(sketch, "E51.12.2", {"start": v(12.5, 6.37) * mm, "end": v(13.7, 6.98) * mm});
            skLineSegment(sketch, "E51.12.3", {"start": v(15.02, 8.35) * mm, "end": v(15.24, 8.7) * mm});
            skLineSegment(sketch, "E51.12.4", {"start": v(14.26, 9.59) * mm, "end": v(14.66, 9.63) * mm});
            skLineSegment(sketch, "E51.12.5", {"start": v(14.66, 9.63) * mm, "end": v(15.1, 9.65) * mm});
            skLineSegment(sketch, "E51.12.6", {"start": v(14.8, 8.06) * mm, "end": v(15.02, 8.35) * mm});
            skLineSegment(sketch, "E51.12.7", {"start": v(15.68, 9.5) * mm, "end": v(15.89, 9.97) * mm});
            skLineSegment(sketch, "E51.12.8", {"start": v(14.6, 7.8) * mm, "end": v(14.8, 8.06) * mm});
            skLineSegment(sketch, "E51.12.9", {"start": v(15.58, 9.65) * mm, "end": v(16.1, 9.63) * mm});
            skLineSegment(sketch, "E51.12.10", {"start": v(15.46, 9.07) * mm, "end": v(15.68, 9.5) * mm});
            skLineSegment(sketch, "E51.12.11", {"start": v(13.9, 9.53) * mm, "end": v(14.26, 9.59) * mm});
            skLineSegment(sketch, "E51.12.12", {"start": v(15.1, 9.65) * mm, "end": v(15.58, 9.65) * mm});
            skLineSegment(sketch, "E51.12.13", {"start": v(14.08, 7.26) * mm, "end": v(14.23, 7.4) * mm});
            skLineSegment(sketch, "E51.12.14", {"start": v(14.23, 7.4) * mm, "end": v(14.4, 7.59) * mm});
            skLineSegment(sketch, "E51.12.15", {"start": v(14.4, 7.59) * mm, "end": v(14.6, 7.8) * mm});
            skLineSegment(sketch, "E51.12.16", {"start": v(13.3, 9.4) * mm, "end": v(13.58, 9.47) * mm});
            skLineSegment(sketch, "E51.12.17", {"start": v(13.06, 9.32) * mm, "end": v(13.3, 9.4) * mm});
            skLineSegment(sketch, "E51.12.18", {"start": v(13.58, 9.47) * mm, "end": v(13.9, 9.53) * mm});
            skLineSegment(sketch, "E51.12.19", {"start": v(13.95, 7.15) * mm, "end": v(14.08, 7.26) * mm});
            skLineSegment(sketch, "E51.12.20", {"start": v(13.84, 7.07) * mm, "end": v(13.95, 7.15) * mm});
            skLineSegment(sketch, "E51.12.21", {"start": v(12.86, 9.25) * mm, "end": v(13.06, 9.32) * mm});
            skLineSegment(sketch, "E51.12.22", {"start": v(12.7, 9.18) * mm, "end": v(12.86, 9.25) * mm});
            skLineSegment(sketch, "E51.12.23", {"start": v(12.5, 9.07) * mm, "end": v(12.58, 9.12) * mm});
            skLineSegment(sketch, "E51.12.24", {"start": v(13.7, 6.98) * mm, "end": v(13.71, 6.99) * mm});
            skLineSegment(sketch, "E51.12.25", {"start": v(13.71, 6.99) * mm, "end": v(13.76, 7.02) * mm});
            skLineSegment(sketch, "E51.12.26", {"start": v(12.58, 9.12) * mm, "end": v(12.7, 9.18) * mm});
            skLineSegment(sketch, "E51.12.27", {"start": v(13.76, 7.02) * mm, "end": v(13.84, 7.07) * mm});
            skLineSegment(sketch, "E51.12.28", {"start": v(12.45, 9.04) * mm, "end": v(12.5, 9.07) * mm});
            skLineSegment(sketch, "E51.12.29", {"start": v(12.43, 9.03) * mm, "end": v(12.45, 9.04) * mm});
            skLineSegment(sketch, "E51.13.0", {"start": v(8.25, 11.36) * mm, "end": v(9.03, 12.43) * mm});
            skLineSegment(sketch, "E51.13.1", {"start": v(11.8, 12.97) * mm, "end": v(11.9, 13.4) * mm});
            skLineSegment(sketch, "E51.13.2", {"start": v(9.93, 9.93) * mm, "end": v(10.87, 10.87) * mm});
            skLineSegment(sketch, "E51.13.3", {"start": v(11.7, 12.58) * mm, "end": v(11.8, 12.97) * mm});
            skLineSegment(sketch, "E51.13.4", {"start": v(10.6, 13.53) * mm, "end": v(10.97, 13.69) * mm});
            skLineSegment(sketch, "E51.13.5", {"start": v(10.97, 13.69) * mm, "end": v(11.38, 13.85) * mm});
            skLineSegment(sketch, "E51.13.6", {"start": v(11.59, 12.24) * mm, "end": v(11.7, 12.58) * mm});
            skLineSegment(sketch, "E51.13.7", {"start": v(11.97, 13.88) * mm, "end": v(12.03, 14.4) * mm});
            skLineSegment(sketch, "E51.13.8", {"start": v(11.47, 11.93) * mm, "end": v(11.59, 12.24) * mm});
            skLineSegment(sketch, "E51.13.9", {"start": v(11.84, 14) * mm, "end": v(12.34, 14.13) * mm});
            skLineSegment(sketch, "E51.13.10", {"start": v(11.9, 13.4) * mm, "end": v(11.97, 13.88) * mm});
            skLineSegment(sketch, "E51.13.11", {"start": v(10.27, 13.36) * mm, "end": v(10.6, 13.53) * mm});
            skLineSegment(sketch, "E51.13.12", {"start": v(11.38, 13.85) * mm, "end": v(11.84, 14) * mm});
            skLineSegment(sketch, "E51.13.13", {"start": v(11.15, 11.26) * mm, "end": v(11.25, 11.44) * mm});
            skLineSegment(sketch, "E51.13.14", {"start": v(11.25, 11.44) * mm, "end": v(11.36, 11.67) * mm});
            skLineSegment(sketch, "E51.13.15", {"start": v(11.36, 11.67) * mm, "end": v(11.47, 11.93) * mm});
            skLineSegment(sketch, "E51.13.16", {"start": v(9.75, 13.04) * mm, "end": v(9.99, 13.2) * mm});
            skLineSegment(sketch, "E51.13.17", {"start": v(9.54, 12.9) * mm, "end": v(9.75, 13.04) * mm});
            skLineSegment(sketch, "E51.13.18", {"start": v(9.99, 13.2) * mm, "end": v(10.27, 13.36) * mm});
            skLineSegment(sketch, "E51.13.19", {"start": v(11.05, 11.11) * mm, "end": v(11.15, 11.26) * mm});
            skLineSegment(sketch, "E51.13.20", {"start": v(10.98, 11) * mm, "end": v(11.05, 11.11) * mm});
            skLineSegment(sketch, "E51.13.21", {"start": v(9.38, 12.77) * mm, "end": v(9.54, 12.9) * mm});
            skLineSegment(sketch, "E51.13.22", {"start": v(9.25, 12.66) * mm, "end": v(9.38, 12.77) * mm});
            skLineSegment(sketch, "E51.13.23", {"start": v(9.08, 12.5) * mm, "end": v(9.15, 12.56) * mm});
            skLineSegment(sketch, "E51.13.24", {"start": v(10.87, 10.87) * mm, "end": v(10.88, 10.88) * mm});
            skLineSegment(sketch, "E51.13.25", {"start": v(10.88, 10.88) * mm, "end": v(10.92, 10.93) * mm});
            skLineSegment(sketch, "E51.13.26", {"start": v(9.15, 12.56) * mm, "end": v(9.25, 12.66) * mm});
            skLineSegment(sketch, "E51.13.27", {"start": v(10.92, 10.93) * mm, "end": v(10.98, 11) * mm});
            skLineSegment(sketch, "E51.13.28", {"start": v(9.05, 12.45) * mm, "end": v(9.08, 12.5) * mm});
            skLineSegment(sketch, "E51.13.29", {"start": v(9.03, 12.43) * mm, "end": v(9.05, 12.45) * mm});
            skLineSegment(sketch, "E51.14.0", {"start": v(4.34, 13.35) * mm, "end": v(4.75, 14.62) * mm});
            skLineSegment(sketch, "E51.14.1", {"start": v(7.22, 15.99) * mm, "end": v(7.17, 16.43) * mm});
            skLineSegment(sketch, "E51.14.2", {"start": v(6.37, 12.5) * mm, "end": v(6.98, 13.7) * mm});
            skLineSegment(sketch, "E51.14.3", {"start": v(7.24, 15.58) * mm, "end": v(7.22, 15.99) * mm});
            skLineSegment(sketch, "E51.14.4", {"start": v(5.9, 16.14) * mm, "end": v(6.2, 16.4) * mm});
            skLineSegment(sketch, "E51.14.5", {"start": v(6.2, 16.4) * mm, "end": v(6.54, 16.69) * mm});
            skLineSegment(sketch, "E51.14.6", {"start": v(7.24, 15.22) * mm, "end": v(7.24, 15.58) * mm});
            skLineSegment(sketch, "E51.14.7", {"start": v(7.1, 16.9) * mm, "end": v(7, 17.4) * mm});
            skLineSegment(sketch, "E51.14.8", {"start": v(7.23, 14.9) * mm, "end": v(7.24, 15.22) * mm});
            skLineSegment(sketch, "E51.14.9", {"start": v(6.93, 16.97) * mm, "end": v(7.37, 17.25) * mm});
            skLineSegment(sketch, "E51.14.10", {"start": v(7.17, 16.43) * mm, "end": v(7.1, 16.9) * mm});
            skLineSegment(sketch, "E51.14.11", {"start": v(5.64, 15.88) * mm, "end": v(5.9, 16.14) * mm});
            skLineSegment(sketch, "E51.14.12", {"start": v(6.54, 16.69) * mm, "end": v(6.93, 16.97) * mm});
            skLineSegment(sketch, "E51.14.13", {"start": v(7.12, 14.15) * mm, "end": v(7.16, 14.36) * mm});
            skLineSegment(sketch, "E51.14.14", {"start": v(7.16, 14.36) * mm, "end": v(7.2, 14.6) * mm});
            skLineSegment(sketch, "E51.14.15", {"start": v(7.2, 14.6) * mm, "end": v(7.23, 14.9) * mm});
            skLineSegment(sketch, "E51.14.16", {"start": v(5.24, 15.42) * mm, "end": v(5.42, 15.64) * mm});
            skLineSegment(sketch, "E51.14.17", {"start": v(5.09, 15.22) * mm, "end": v(5.24, 15.42) * mm});
            skLineSegment(sketch, "E51.14.18", {"start": v(5.42, 15.64) * mm, "end": v(5.64, 15.88) * mm});
            skLineSegment(sketch, "E51.14.19", {"start": v(7.08, 13.98) * mm, "end": v(7.12, 14.15) * mm});
            skLineSegment(sketch, "E51.14.20", {"start": v(7.04, 13.86) * mm, "end": v(7.08, 13.98) * mm});
            skLineSegment(sketch, "E51.14.21", {"start": v(4.97, 15.04) * mm, "end": v(5.09, 15.22) * mm});
            skLineSegment(sketch, "E51.14.22", {"start": v(4.88, 14.9) * mm, "end": v(4.97, 15.04) * mm});
            skLineSegment(sketch, "E51.14.23", {"start": v(4.78, 14.69) * mm, "end": v(4.82, 14.78) * mm});
            skLineSegment(sketch, "E51.14.24", {"start": v(6.98, 13.7) * mm, "end": v(6.99, 13.71) * mm});
            skLineSegment(sketch, "E51.14.25", {"start": v(6.99, 13.71) * mm, "end": v(7, 13.76) * mm});
            skLineSegment(sketch, "E51.14.26", {"start": v(4.82, 14.78) * mm, "end": v(4.88, 14.9) * mm});
            skLineSegment(sketch, "E51.14.27", {"start": v(7, 13.76) * mm, "end": v(7.04, 13.86) * mm});
            skLineSegment(sketch, "E51.14.28", {"start": v(4.76, 14.64) * mm, "end": v(4.78, 14.69) * mm});
            skLineSegment(sketch, "E51.14.29", {"start": v(4.75, 14.62) * mm, "end": v(4.76, 14.64) * mm});
            skLineSegment(sketch, "E51.15.0", {"start": v(0, 14.04) * mm, "end": v(0, 15.37) * mm});
            skLineSegment(sketch, "E51.15.1", {"start": v(1.92, 17.43) * mm, "end": v(1.74, 17.84) * mm});
            skLineSegment(sketch, "E51.15.2", {"start": v(2.2, 13.87) * mm, "end": v(2.4, 15.18) * mm});
            skLineSegment(sketch, "E51.15.3", {"start": v(2.07, 17.06) * mm, "end": v(1.92, 17.43) * mm});
            skLineSegment(sketch, "E51.15.4", {"start": v(0.62, 17.17) * mm, "end": v(0.83, 17.52) * mm});
            skLineSegment(sketch, "E51.15.5", {"start": v(0.83, 17.52) * mm, "end": v(1.07, 17.9) * mm});
            skLineSegment(sketch, "E51.15.6", {"start": v(2.18, 16.71) * mm, "end": v(2.07, 17.06) * mm});
            skLineSegment(sketch, "E51.15.7", {"start": v(1.53, 18.27) * mm, "end": v(1.27, 18.72) * mm});
            skLineSegment(sketch, "E51.15.8", {"start": v(2.27, 16.4) * mm, "end": v(2.18, 16.71) * mm});
            skLineSegment(sketch, "E51.15.9", {"start": v(1.35, 18.28) * mm, "end": v(1.67, 18.69) * mm});
            skLineSegment(sketch, "E51.15.10", {"start": v(1.74, 17.84) * mm, "end": v(1.53, 18.27) * mm});
            skLineSegment(sketch, "E51.15.11", {"start": v(0.46, 16.85) * mm, "end": v(0.62, 17.17) * mm});
            skLineSegment(sketch, "E51.15.12", {"start": v(1.07, 17.9) * mm, "end": v(1.35, 18.28) * mm});
            skLineSegment(sketch, "E51.15.13", {"start": v(2.4, 15.66) * mm, "end": v(2.37, 15.87) * mm});
            skLineSegment(sketch, "E51.15.14", {"start": v(2.37, 15.87) * mm, "end": v(2.33, 16.12) * mm});
            skLineSegment(sketch, "E51.15.15", {"start": v(2.33, 16.12) * mm, "end": v(2.27, 16.4) * mm});
            skLineSegment(sketch, "E51.15.16", {"start": v(0.22, 16.28) * mm, "end": v(0.32, 16.55) * mm});
            skLineSegment(sketch, "E51.15.17", {"start": v(0.14, 16.05) * mm, "end": v(0.22, 16.28) * mm});
            skLineSegment(sketch, "E51.15.18", {"start": v(0.32, 16.55) * mm, "end": v(0.46, 16.85) * mm});
            skLineSegment(sketch, "E51.15.19", {"start": v(2.41, 15.49) * mm, "end": v(2.4, 15.66) * mm});
            skLineSegment(sketch, "E51.15.20", {"start": v(2.41, 15.35) * mm, "end": v(2.41, 15.49) * mm});
            skLineSegment(sketch, "E51.15.21", {"start": v(0.08, 15.84) * mm, "end": v(0.14, 16.05) * mm});
            skLineSegment(sketch, "E51.15.22", {"start": v(0.04, 15.67) * mm, "end": v(0.08, 15.84) * mm});
            skLineSegment(sketch, "E51.15.23", {"start": v(0, 15.45) * mm, "end": v(0.02, 15.54) * mm});
            skLineSegment(sketch, "E51.15.24", {"start": v(2.4, 15.18) * mm, "end": v(2.4, 15.2) * mm});
            skLineSegment(sketch, "E51.15.25", {"start": v(2.4, 15.2) * mm, "end": v(2.41, 15.26) * mm});
            skLineSegment(sketch, "E51.15.26", {"start": v(0.02, 15.54) * mm, "end": v(0.04, 15.67) * mm});
            skLineSegment(sketch, "E51.15.27", {"start": v(2.41, 15.26) * mm, "end": v(2.41, 15.35) * mm});
            skLineSegment(sketch, "E51.15.28", {"start": v(0, 15.39) * mm, "end": v(0, 15.45) * mm});
            skLineSegment(sketch, "E51.15.29", {"start": v(0, 15.37) * mm, "end": v(0, 15.39) * mm});
            skLineSegment(sketch, "E51.16.0", {"start": v(-4.34, 13.35) * mm, "end": v(-4.75, 14.62) * mm});
            skLineSegment(sketch, "E51.16.1", {"start": v(-3.56, 17.18) * mm, "end": v(-3.85, 17.5) * mm});
            skLineSegment(sketch, "E51.16.2", {"start": v(-2.2, 13.87) * mm, "end": v(-2.4, 15.18) * mm});
            skLineSegment(sketch, "E51.16.3", {"start": v(-3.3, 16.86) * mm, "end": v(-3.56, 17.18) * mm});
            skLineSegment(sketch, "E51.16.4", {"start": v(-4.71, 16.52) * mm, "end": v(-4.63, 16.92) * mm});
            skLineSegment(sketch, "E51.16.5", {"start": v(-4.63, 16.92) * mm, "end": v(-4.51, 17.35) * mm});
            skLineSegment(sketch, "E51.16.6", {"start": v(-3.09, 16.57) * mm, "end": v(-3.3, 16.86) * mm});
            skLineSegment(sketch, "E51.16.7", {"start": v(-4.2, 17.85) * mm, "end": v(-4.58, 18.2) * mm});
            skLineSegment(sketch, "E51.16.8", {"start": v(-2.9, 16.3) * mm, "end": v(-3.09, 16.57) * mm});
            skLineSegment(sketch, "E51.16.9", {"start": v(-4.37, 17.8) * mm, "end": v(-4.18, 18.29) * mm});
            skLineSegment(sketch, "E51.16.10", {"start": v(-3.85, 17.5) * mm, "end": v(-4.2, 17.85) * mm});
            skLineSegment(sketch, "E51.16.11", {"start": v(-4.77, 16.16) * mm, "end": v(-4.71, 16.52) * mm});
            skLineSegment(sketch, "E51.16.12", {"start": v(-4.51, 17.35) * mm, "end": v(-4.37, 17.8) * mm});
            skLineSegment(sketch, "E51.16.13", {"start": v(-2.56, 15.63) * mm, "end": v(-2.65, 15.83) * mm});
            skLineSegment(sketch, "E51.16.14", {"start": v(-2.65, 15.83) * mm, "end": v(-2.76, 16.05) * mm});
            skLineSegment(sketch, "E51.16.15", {"start": v(-2.76, 16.05) * mm, "end": v(-2.9, 16.3) * mm});
            skLineSegment(sketch, "E51.16.16", {"start": v(-4.83, 15.55) * mm, "end": v(-4.8, 15.84) * mm});
            skLineSegment(sketch, "E51.16.17", {"start": v(-4.83, 15.3) * mm, "end": v(-4.83, 15.55) * mm});
            skLineSegment(sketch, "E51.16.18", {"start": v(-4.8, 15.84) * mm, "end": v(-4.77, 16.16) * mm});
            skLineSegment(sketch, "E51.16.19", {"start": v(-2.5, 15.47) * mm, "end": v(-2.56, 15.63) * mm});
            skLineSegment(sketch, "E51.16.20", {"start": v(-2.45, 15.35) * mm, "end": v(-2.5, 15.47) * mm});
            skLineSegment(sketch, "E51.16.21", {"start": v(-4.82, 15.1) * mm, "end": v(-4.83, 15.3) * mm});
            skLineSegment(sketch, "E51.16.22", {"start": v(-4.8, 14.92) * mm, "end": v(-4.82, 15.1) * mm});
            skLineSegment(sketch, "E51.16.23", {"start": v(-4.77, 14.7) * mm, "end": v(-4.79, 14.79) * mm});
            skLineSegment(sketch, "E51.16.24", {"start": v(-2.4, 15.18) * mm, "end": v(-2.4, 15.2) * mm});
            skLineSegment(sketch, "E51.16.25", {"start": v(-2.4, 15.2) * mm, "end": v(-2.42, 15.26) * mm});
            skLineSegment(sketch, "E51.16.26", {"start": v(-4.79, 14.79) * mm, "end": v(-4.8, 14.92) * mm});
            skLineSegment(sketch, "E51.16.27", {"start": v(-2.42, 15.26) * mm, "end": v(-2.45, 15.35) * mm});
            skLineSegment(sketch, "E51.16.28", {"start": v(-4.75, 14.64) * mm, "end": v(-4.77, 14.7) * mm});
            skLineSegment(sketch, "E51.16.29", {"start": v(-4.75, 14.62) * mm, "end": v(-4.75, 14.64) * mm});
            skLineSegment(sketch, "E51.17.0", {"start": v(-8.25, 11.36) * mm, "end": v(-9.03, 12.43) * mm});
            skLineSegment(sketch, "E51.17.1", {"start": v(-8.7, 15.24) * mm, "end": v(-9.07, 15.46) * mm});
            skLineSegment(sketch, "E51.17.2", {"start": v(-6.37, 12.5) * mm, "end": v(-6.98, 13.7) * mm});
            skLineSegment(sketch, "E51.17.3", {"start": v(-8.35, 15.02) * mm, "end": v(-8.7, 15.24) * mm});
            skLineSegment(sketch, "E51.17.4", {"start": v(-9.59, 14.26) * mm, "end": v(-9.63, 14.66) * mm});
            skLineSegment(sketch, "E51.17.5", {"start": v(-9.63, 14.66) * mm, "end": v(-9.65, 15.1) * mm});
            skLineSegment(sketch, "E51.17.6", {"start": v(-8.06, 14.8) * mm, "end": v(-8.35, 15.02) * mm});
            skLineSegment(sketch, "E51.17.7", {"start": v(-9.5, 15.68) * mm, "end": v(-9.97, 15.89) * mm});
            skLineSegment(sketch, "E51.17.8", {"start": v(-7.8, 14.6) * mm, "end": v(-8.06, 14.8) * mm});
            skLineSegment(sketch, "E51.17.9", {"start": v(-9.65, 15.58) * mm, "end": v(-9.63, 16.1) * mm});
            skLineSegment(sketch, "E51.17.10", {"start": v(-9.07, 15.46) * mm, "end": v(-9.5, 15.68) * mm});
            skLineSegment(sketch, "E51.17.11", {"start": v(-9.53, 13.9) * mm, "end": v(-9.59, 14.26) * mm});
            skLineSegment(sketch, "E51.17.12", {"start": v(-9.65, 15.1) * mm, "end": v(-9.65, 15.58) * mm});
            skLineSegment(sketch, "E51.17.13", {"start": v(-7.26, 14.08) * mm, "end": v(-7.4, 14.23) * mm});
            skLineSegment(sketch, "E51.17.14", {"start": v(-7.4, 14.23) * mm, "end": v(-7.59, 14.4) * mm});
            skLineSegment(sketch, "E51.17.15", {"start": v(-7.59, 14.4) * mm, "end": v(-7.8, 14.6) * mm});
            skLineSegment(sketch, "E51.17.16", {"start": v(-9.4, 13.3) * mm, "end": v(-9.47, 13.58) * mm});
            skLineSegment(sketch, "E51.17.17", {"start": v(-9.32, 13.06) * mm, "end": v(-9.4, 13.3) * mm});
            skLineSegment(sketch, "E51.17.18", {"start": v(-9.47, 13.58) * mm, "end": v(-9.53, 13.9) * mm});
            skLineSegment(sketch, "E51.17.19", {"start": v(-7.15, 13.95) * mm, "end": v(-7.26, 14.08) * mm});
            skLineSegment(sketch, "E51.17.20", {"start": v(-7.07, 13.84) * mm, "end": v(-7.15, 13.95) * mm});
            skLineSegment(sketch, "E51.17.21", {"start": v(-9.25, 12.86) * mm, "end": v(-9.32, 13.06) * mm});
            skLineSegment(sketch, "E51.17.22", {"start": v(-9.18, 12.7) * mm, "end": v(-9.25, 12.86) * mm});
            skLineSegment(sketch, "E51.17.23", {"start": v(-9.07, 12.5) * mm, "end": v(-9.12, 12.58) * mm});
            skLineSegment(sketch, "E51.17.24", {"start": v(-6.98, 13.7) * mm, "end": v(-6.99, 13.71) * mm});
            skLineSegment(sketch, "E51.17.25", {"start": v(-6.99, 13.71) * mm, "end": v(-7.02, 13.76) * mm});
            skLineSegment(sketch, "E51.17.26", {"start": v(-9.12, 12.58) * mm, "end": v(-9.18, 12.7) * mm});
            skLineSegment(sketch, "E51.17.27", {"start": v(-7.02, 13.76) * mm, "end": v(-7.07, 13.84) * mm});
            skLineSegment(sketch, "E51.17.28", {"start": v(-9.04, 12.45) * mm, "end": v(-9.07, 12.5) * mm});
            skLineSegment(sketch, "E51.17.29", {"start": v(-9.03, 12.43) * mm, "end": v(-9.04, 12.45) * mm});
            skLineSegment(sketch, "E51.18.0", {"start": v(-11.36, 8.25) * mm, "end": v(-12.43, 9.03) * mm});
            skLineSegment(sketch, "E51.18.1", {"start": v(-12.97, 11.8) * mm, "end": v(-13.4, 11.9) * mm});
            skLineSegment(sketch, "E51.18.2", {"start": v(-9.93, 9.93) * mm, "end": v(-10.87, 10.87) * mm});
            skLineSegment(sketch, "E51.18.3", {"start": v(-12.58, 11.7) * mm, "end": v(-12.97, 11.8) * mm});
            skLineSegment(sketch, "E51.18.4", {"start": v(-13.53, 10.6) * mm, "end": v(-13.69, 10.97) * mm});
            skLineSegment(sketch, "E51.18.5", {"start": v(-13.69, 10.97) * mm, "end": v(-13.85, 11.38) * mm});
            skLineSegment(sketch, "E51.18.6", {"start": v(-12.24, 11.59) * mm, "end": v(-12.58, 11.7) * mm});
            skLineSegment(sketch, "E51.18.7", {"start": v(-13.88, 11.97) * mm, "end": v(-14.4, 12.03) * mm});
            skLineSegment(sketch, "E51.18.8", {"start": v(-11.93, 11.47) * mm, "end": v(-12.24, 11.59) * mm});
            skLineSegment(sketch, "E51.18.9", {"start": v(-14, 11.84) * mm, "end": v(-14.13, 12.34) * mm});
            skLineSegment(sketch, "E51.18.10", {"start": v(-13.4, 11.9) * mm, "end": v(-13.88, 11.97) * mm});
            skLineSegment(sketch, "E51.18.11", {"start": v(-13.36, 10.27) * mm, "end": v(-13.53, 10.6) * mm});
            skLineSegment(sketch, "E51.18.12", {"start": v(-13.85, 11.38) * mm, "end": v(-14, 11.84) * mm});
            skLineSegment(sketch, "E51.18.13", {"start": v(-11.26, 11.15) * mm, "end": v(-11.44, 11.25) * mm});
            skLineSegment(sketch, "E51.18.14", {"start": v(-11.44, 11.25) * mm, "end": v(-11.67, 11.36) * mm});
            skLineSegment(sketch, "E51.18.15", {"start": v(-11.67, 11.36) * mm, "end": v(-11.93, 11.47) * mm});
            skLineSegment(sketch, "E51.18.16", {"start": v(-13.04, 9.75) * mm, "end": v(-13.2, 9.99) * mm});
            skLineSegment(sketch, "E51.18.17", {"start": v(-12.9, 9.54) * mm, "end": v(-13.04, 9.75) * mm});
            skLineSegment(sketch, "E51.18.18", {"start": v(-13.2, 9.99) * mm, "end": v(-13.36, 10.27) * mm});
            skLineSegment(sketch, "E51.18.19", {"start": v(-11.11, 11.05) * mm, "end": v(-11.26, 11.15) * mm});
            skLineSegment(sketch, "E51.18.20", {"start": v(-11, 10.98) * mm, "end": v(-11.11, 11.05) * mm});
            skLineSegment(sketch, "E51.18.21", {"start": v(-12.77, 9.38) * mm, "end": v(-12.9, 9.54) * mm});
            skLineSegment(sketch, "E51.18.22", {"start": v(-12.66, 9.25) * mm, "end": v(-12.77, 9.38) * mm});
            skLineSegment(sketch, "E51.18.23", {"start": v(-12.5, 9.08) * mm, "end": v(-12.56, 9.15) * mm});
            skLineSegment(sketch, "E51.18.24", {"start": v(-10.87, 10.87) * mm, "end": v(-10.88, 10.88) * mm});
            skLineSegment(sketch, "E51.18.25", {"start": v(-10.88, 10.88) * mm, "end": v(-10.93, 10.92) * mm});
            skLineSegment(sketch, "E51.18.26", {"start": v(-12.56, 9.15) * mm, "end": v(-12.66, 9.25) * mm});
            skLineSegment(sketch, "E51.18.27", {"start": v(-10.93, 10.92) * mm, "end": v(-11, 10.98) * mm});
            skLineSegment(sketch, "E51.18.28", {"start": v(-12.45, 9.05) * mm, "end": v(-12.5, 9.08) * mm});
            skLineSegment(sketch, "E51.18.29", {"start": v(-12.43, 9.03) * mm, "end": v(-12.45, 9.05) * mm});
            skLineSegment(sketch, "E51.19.0", {"start": v(-13.35, 4.34) * mm, "end": v(-14.62, 4.75) * mm});
            skLineSegment(sketch, "E51.19.1", {"start": v(-15.99, 7.22) * mm, "end": v(-16.43, 7.17) * mm});
            skLineSegment(sketch, "E51.19.2", {"start": v(-12.5, 6.37) * mm, "end": v(-13.7, 6.98) * mm});
            skLineSegment(sketch, "E51.19.3", {"start": v(-15.58, 7.24) * mm, "end": v(-15.99, 7.22) * mm});
            skLineSegment(sketch, "E51.19.4", {"start": v(-16.14, 5.9) * mm, "end": v(-16.4, 6.2) * mm});
            skLineSegment(sketch, "E51.19.5", {"start": v(-16.4, 6.2) * mm, "end": v(-16.69, 6.54) * mm});
            skLineSegment(sketch, "E51.19.6", {"start": v(-15.22, 7.24) * mm, "end": v(-15.58, 7.24) * mm});
            skLineSegment(sketch, "E51.19.7", {"start": v(-16.9, 7.1) * mm, "end": v(-17.4, 7) * mm});
            skLineSegment(sketch, "E51.19.8", {"start": v(-14.9, 7.23) * mm, "end": v(-15.22, 7.24) * mm});
            skLineSegment(sketch, "E51.19.9", {"start": v(-16.97, 6.93) * mm, "end": v(-17.25, 7.37) * mm});
            skLineSegment(sketch, "E51.19.10", {"start": v(-16.43, 7.17) * mm, "end": v(-16.9, 7.1) * mm});
            skLineSegment(sketch, "E51.19.11", {"start": v(-15.88, 5.64) * mm, "end": v(-16.14, 5.9) * mm});
            skLineSegment(sketch, "E51.19.12", {"start": v(-16.69, 6.54) * mm, "end": v(-16.97, 6.93) * mm});
            skLineSegment(sketch, "E51.19.13", {"start": v(-14.15, 7.12) * mm, "end": v(-14.36, 7.16) * mm});
            skLineSegment(sketch, "E51.19.14", {"start": v(-14.36, 7.16) * mm, "end": v(-14.6, 7.2) * mm});
            skLineSegment(sketch, "E51.19.15", {"start": v(-14.6, 7.2) * mm, "end": v(-14.9, 7.23) * mm});
            skLineSegment(sketch, "E51.19.16", {"start": v(-15.42, 5.24) * mm, "end": v(-15.64, 5.42) * mm});
            skLineSegment(sketch, "E51.19.17", {"start": v(-15.22, 5.09) * mm, "end": v(-15.42, 5.24) * mm});
            skLineSegment(sketch, "E51.19.18", {"start": v(-15.64, 5.42) * mm, "end": v(-15.88, 5.64) * mm});
            skLineSegment(sketch, "E51.19.19", {"start": v(-13.98, 7.08) * mm, "end": v(-14.15, 7.12) * mm});
            skLineSegment(sketch, "E51.19.20", {"start": v(-13.86, 7.04) * mm, "end": v(-13.98, 7.08) * mm});
            skLineSegment(sketch, "E51.19.21", {"start": v(-15.04, 4.97) * mm, "end": v(-15.22, 5.09) * mm});
            skLineSegment(sketch, "E51.19.22", {"start": v(-14.9, 4.88) * mm, "end": v(-15.04, 4.97) * mm});
            skLineSegment(sketch, "E51.19.23", {"start": v(-14.69, 4.78) * mm, "end": v(-14.78, 4.82) * mm});
            skLineSegment(sketch, "E51.19.24", {"start": v(-13.7, 6.98) * mm, "end": v(-13.71, 6.99) * mm});
            skLineSegment(sketch, "E51.19.25", {"start": v(-13.71, 6.99) * mm, "end": v(-13.76, 7) * mm});
            skLineSegment(sketch, "E51.19.26", {"start": v(-14.78, 4.82) * mm, "end": v(-14.9, 4.88) * mm});
            skLineSegment(sketch, "E51.19.27", {"start": v(-13.76, 7) * mm, "end": v(-13.86, 7.04) * mm});
            skLineSegment(sketch, "E51.19.28", {"start": v(-14.64, 4.76) * mm, "end": v(-14.69, 4.78) * mm});
            skLineSegment(sketch, "E51.19.29", {"start": v(-14.62, 4.75) * mm, "end": v(-14.64, 4.76) * mm});
            skSolve(sketch);
        }
        {
            var Q0;
            {var subQ0=sQuery(id+"F1.wireOp",EDGE,"E0");var subQ27=makeQuery(id+"F1.imprint","INTERSECT",VERTEX,{"derivedFrom":[subQ0,sQuery(id+"F1.wireOp",EDGE,"E51.10.0")]});Q0=makeQuery(id+"F1.imprint","IMPRINT",FACE,{"disambiguationData":[TD([[makeQuery(id+"F1.imprint","IMPRINT",EDGE,{"disambiguationData":[TD([[subQ27,-1.0]])],"derivedFrom":subQ0}),1.0]])]});}
            var Q1;
            {var subQ0=sQuery(id+"F1.wireOp",EDGE,"E51.1.0");Q1=makeQuery(id+"F1.imprint","IMPRINT",FACE,{"disambiguationData":[TD([[makeQuery(id+"F1.imprint","IMPRINT",EDGE,{"derivedFrom":subQ0}),-1.0]])]});}
            var Q2;
            {var subQ7=sQuery(id+"F1.wireOp",EDGE,"E51.2.0");Q2=makeQuery(id+"F1.imprint","IMPRINT",FACE,{"disambiguationData":[TD([[makeQuery(id+"F1.imprint","IMPRINT",EDGE,{"derivedFrom":subQ7}),-1.0]])]});}
            var Q3;
            {var subQ8=sQuery(id+"F1.wireOp",EDGE,"E51.3.0");Q3=makeQuery(id+"F1.imprint","IMPRINT",FACE,{"disambiguationData":[TD([[makeQuery(id+"F1.imprint","IMPRINT",EDGE,{"derivedFrom":subQ8}),-1.0]])]});}
            var Q4;
            {var subQ2=sQuery(id+"F1.wireOp",EDGE,"E51.4.0");Q4=makeQuery(id+"F1.imprint","IMPRINT",FACE,{"disambiguationData":[TD([[makeQuery(id+"F1.imprint","IMPRINT",EDGE,{"derivedFrom":subQ2}),-1.0]])]});}
            var Q5;
            {var subQ8=sQuery(id+"F1.wireOp",EDGE,"E51.5.0");Q5=makeQuery(id+"F1.imprint","IMPRINT",FACE,{"disambiguationData":[TD([[makeQuery(id+"F1.imprint","IMPRINT",EDGE,{"derivedFrom":subQ8}),-1.0]])]});}
            var Q6;
            {var subQ3=sQuery(id+"F1.wireOp",EDGE,"E51.6.0");Q6=makeQuery(id+"F1.imprint","IMPRINT",FACE,{"disambiguationData":[TD([[makeQuery(id+"F1.imprint","IMPRINT",EDGE,{"derivedFrom":subQ3}),-1.0]])]});}
            var Q7;
            {var subQ0=sQuery(id+"F1.wireOp",EDGE,"E51.7.0");Q7=makeQuery(id+"F1.imprint","IMPRINT",FACE,{"disambiguationData":[TD([[makeQuery(id+"F1.imprint","IMPRINT",EDGE,{"derivedFrom":subQ0}),-1.0]])]});}
            var Q8;
            {var subQ5=sQuery(id+"F1.wireOp",EDGE,"E51.8.0");Q8=makeQuery(id+"F1.imprint","IMPRINT",FACE,{"disambiguationData":[TD([[makeQuery(id+"F1.imprint","IMPRINT",EDGE,{"derivedFrom":subQ5}),-1.0]])]});}
            var Q9;
            {var subQ1=sQuery(id+"F1.wireOp",EDGE,"E51.9.0");Q9=makeQuery(id+"F1.imprint","IMPRINT",FACE,{"disambiguationData":[TD([[makeQuery(id+"F1.imprint","IMPRINT",EDGE,{"derivedFrom":subQ1}),-1.0]])]});}
            var Q10;
            {var subQ5=sQuery(id+"F1.wireOp",EDGE,"E51.10.0");Q10=makeQuery(id+"F1.imprint","IMPRINT",FACE,{"disambiguationData":[TD([[makeQuery(id+"F1.imprint","IMPRINT",EDGE,{"derivedFrom":subQ5}),-1.0]])]});}
            var Q11;
            {var subQ8=sQuery(id+"F1.wireOp",EDGE,"E51.11.0");Q11=makeQuery(id+"F1.imprint","IMPRINT",FACE,{"disambiguationData":[TD([[makeQuery(id+"F1.imprint","IMPRINT",EDGE,{"derivedFrom":subQ8}),-1.0]])]});}
            var Q12;
            {var subQ2=sQuery(id+"F1.wireOp",EDGE,"E51.12.0");Q12=makeQuery(id+"F1.imprint","IMPRINT",FACE,{"disambiguationData":[TD([[makeQuery(id+"F1.imprint","IMPRINT",EDGE,{"derivedFrom":subQ2}),-1.0]])]});}
            var Q13;
            {var subQ3=sQuery(id+"F1.wireOp",EDGE,"E51.13.0");Q13=makeQuery(id+"F1.imprint","IMPRINT",FACE,{"disambiguationData":[TD([[makeQuery(id+"F1.imprint","IMPRINT",EDGE,{"derivedFrom":subQ3}),-1.0]])]});}
            var Q14;
            {var subQ0=sQuery(id+"F1.wireOp",EDGE,"E51.14.0");Q14=makeQuery(id+"F1.imprint","IMPRINT",FACE,{"disambiguationData":[TD([[makeQuery(id+"F1.imprint","IMPRINT",EDGE,{"derivedFrom":subQ0}),-1.0]])]});}
            var Q15;
            {var subQ6=sQuery(id+"F1.wireOp",EDGE,"E51.15.0");Q15=makeQuery(id+"F1.imprint","IMPRINT",FACE,{"disambiguationData":[TD([[makeQuery(id+"F1.imprint","IMPRINT",EDGE,{"derivedFrom":subQ6}),-1.0]])]});}
            var Q16;
            {var subQ5=sQuery(id+"F1.wireOp",EDGE,"E51.16.0");Q16=makeQuery(id+"F1.imprint","IMPRINT",FACE,{"disambiguationData":[TD([[makeQuery(id+"F1.imprint","IMPRINT",EDGE,{"derivedFrom":subQ5}),-1.0]])]});}
            var Q17;
            {var subQ7=sQuery(id+"F1.wireOp",EDGE,"E51.17.0");Q17=makeQuery(id+"F1.imprint","IMPRINT",FACE,{"disambiguationData":[TD([[makeQuery(id+"F1.imprint","IMPRINT",EDGE,{"derivedFrom":subQ7}),-1.0]])]});}
            var Q18;
            {var subQ5=sQuery(id+"F1.wireOp",EDGE,"E51.18.0");Q18=makeQuery(id+"F1.imprint","IMPRINT",FACE,{"disambiguationData":[TD([[makeQuery(id+"F1.imprint","IMPRINT",EDGE,{"derivedFrom":subQ5}),-1.0]])]});}
            var Q19;
            {var subQ8=sQuery(id+"F1.wireOp",EDGE,"E51.19.0");Q19=makeQuery(id+"F1.imprint","IMPRINT",FACE,{"disambiguationData":[TD([[makeQuery(id+"F1.imprint","IMPRINT",EDGE,{"derivedFrom":subQ8}),-1.0]])]});}
            var Q20;
            {var subQ8=sQuery(id+"F1.wireOp",EDGE,"E21");Q20=makeQuery(id+"F1.imprint","IMPRINT",FACE,{"disambiguationData":[TD([[makeQuery(id+"F1.imprint","IMPRINT",EDGE,{"derivedFrom":subQ8}),-1.0]])]});}
            extrude(context, id + "F2", {"entities" : qUnion([Q0, Q1, Q2, Q3, Q4, Q5, Q6, Q7, Q8, Q9, Q10, Q11, Q12, Q13, Q14, Q15, Q16, Q17, Q18, Q19, Q20]), "depth" : (getVariable(context, 'GearThickness')) * mm});
        }
    });
